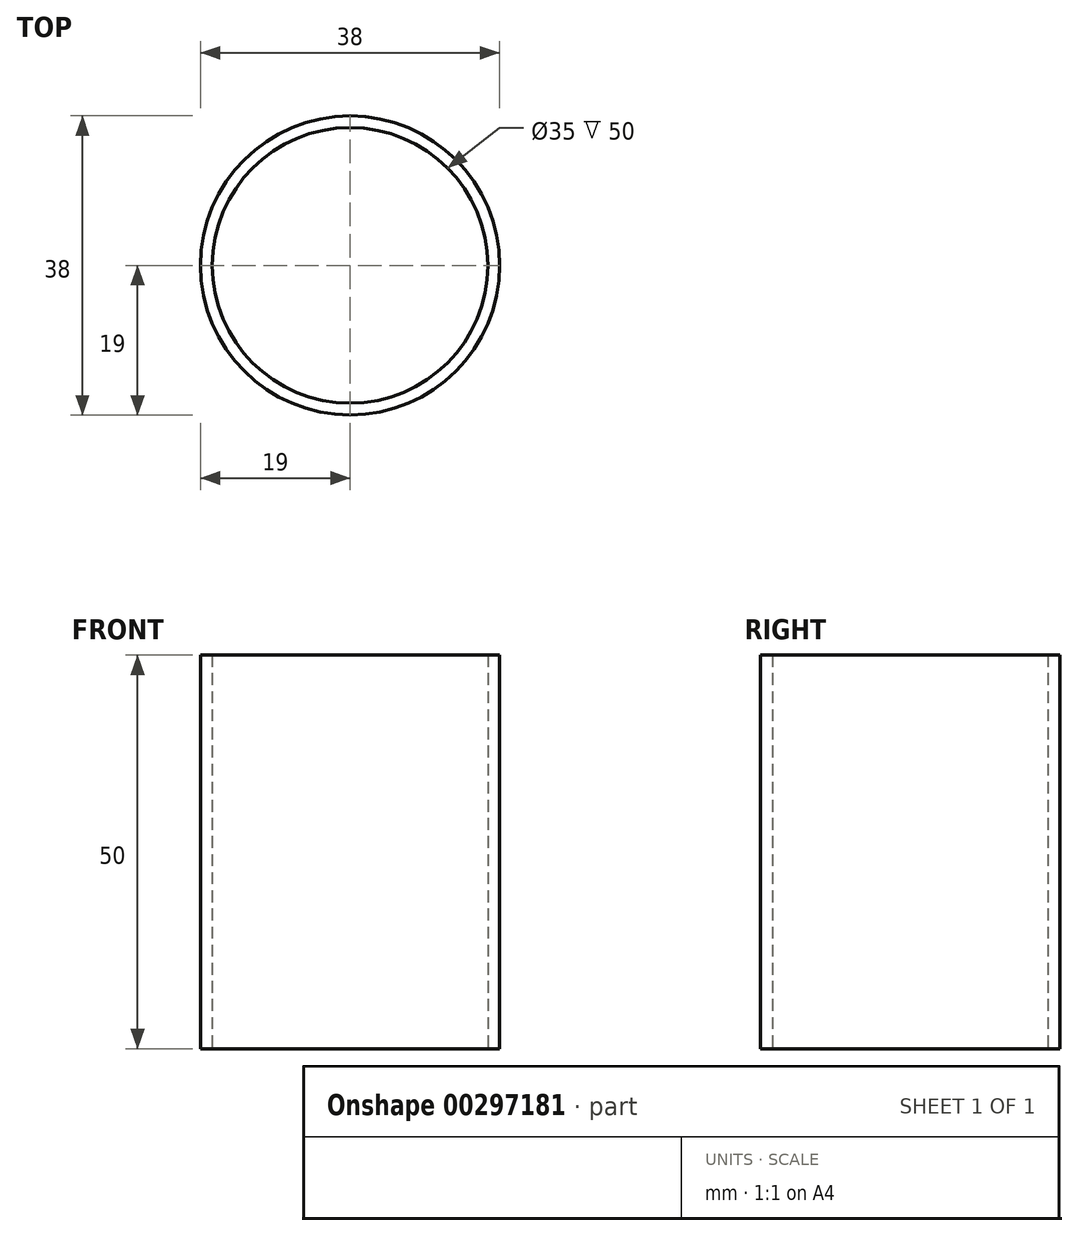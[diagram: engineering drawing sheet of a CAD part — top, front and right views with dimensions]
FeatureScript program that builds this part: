
annotation { "Feature Type Name" : "Feature", "Feature Type Description" : "" }
export const myFeature = defineFeature(function(context is Context, id is Id, definition is map)
    precondition{}
    {
        {
            var Q0;
            Q0=qCreatedBy(makeId("Top.planeOp"),FACE);
            var sketch = newSketch(context, id + "F0", { "sketchPlane" : qUnion([Q0])});
            skCircle(sketch, "E0", {"center": v(0, 0) * mm, "radius": 19 * mm});
            skCircle(sketch, "E1", {"center": v(0, 0) * mm, "radius": 17.5 * mm});
            skSolve(sketch);
        }
        {
            var Q0;
            Q0 = qSketchRegion(id + "F0", true);
            extrude(context, id + "F1", {"entities" : qUnion([Q0]), "depth" : 50 * mm});
        }
    });
